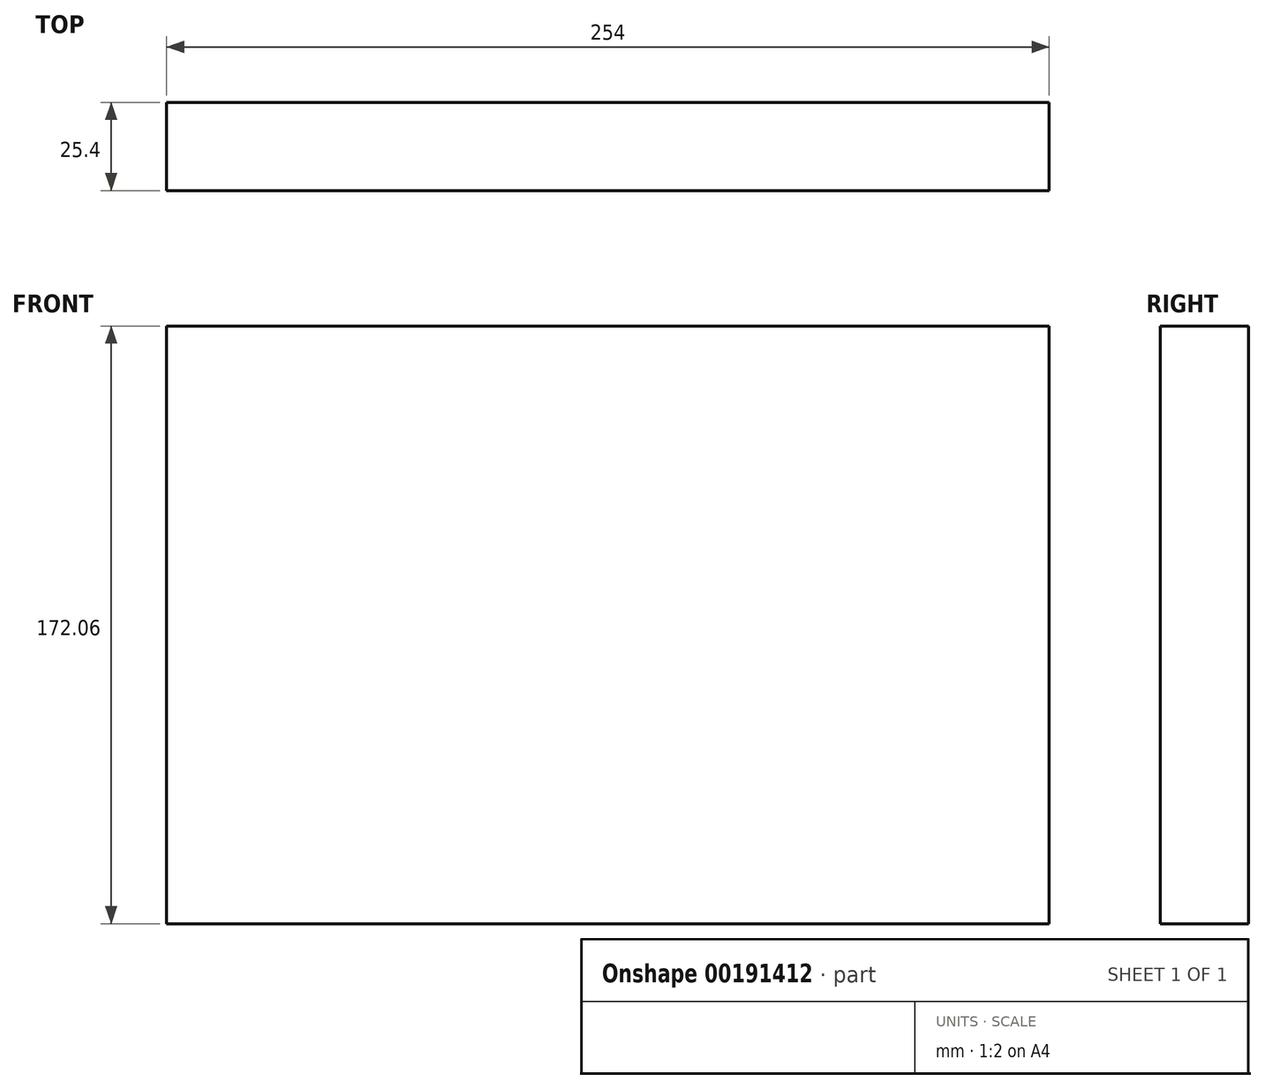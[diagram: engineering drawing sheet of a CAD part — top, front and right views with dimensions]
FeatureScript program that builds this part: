
annotation { "Feature Type Name" : "Feature", "Feature Type Description" : "" }
export const myFeature = defineFeature(function(context is Context, id is Id, definition is map)
    precondition{}
    {
        {
            var Q0;
            Q0=qCreatedBy(makeId("Front.planeOp"),FACE);
            var sketch = newSketch(context, id + "F0", { "sketchPlane" : qUnion([Q0])});
            skLineSegment(sketch, "E0.bottom", {"start": v(-155.61, 110.9) * mm, "end": v(98.39, 110.9) * mm});
            skLineSegment(sketch, "E0.top", {"start": v(-155.61, -61.17) * mm, "end": v(98.39, -61.17) * mm});
            skLineSegment(sketch, "E0.left", {"start": v(-155.61, 110.9) * mm, "end": v(-155.61, -61.17) * mm});
            skLineSegment(sketch, "E0.right", {"start": v(98.39, 110.9) * mm, "end": v(98.39, -61.17) * mm});
            skSolve(sketch);
        }
        {
            var Q0;
            Q0=makeQuery(id+"F0.imprint","IMPRINT",FACE,{"disambiguationData":[TD([[makeQuery(id+"F0.imprint","IMPRINT",EDGE,{"derivedFrom":sQuery(id+"F0.wireOp",EDGE,"E0.bottom")}),-1.0]])]});
            extrude(context, id + "F1", {"entities" : qUnion([Q0]), "depth" : 25.4 * mm});
        }
    });
